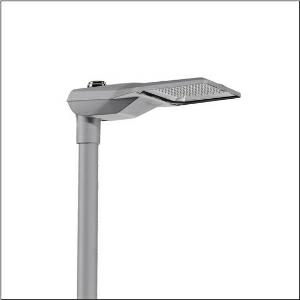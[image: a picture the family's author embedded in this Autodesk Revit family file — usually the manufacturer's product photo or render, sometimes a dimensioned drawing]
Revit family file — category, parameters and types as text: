
# Revit family: streetlight_sl_21_midi___p0_8a_5xe7u47n08lb_d940
name_source: partatom
category: Lighting Fixtures
units: mm (PartAtom-declared; Revit-internal decimal feet)

## family parameters
Cut with Voids When Loaded = No
Host = Face
Light Source = No
Part Type = Normal
Room Calculation Point = No
Round Connector Dimension = Use Diameter
Shared = No

## types (1)
- --- (1 x LED, 15080 lm, 98.3 W, 4000K)
    Apparent Load = 98 VA
    CIE Flux Codes = 33 69 96 100 100
    Color Rendering = 70
    Color Temperature = 4000K
    Default Elevation = 1800 mm
    Description = Streetlight SL 21 midi, mast luminaire, primary light control with lens, of PMMA, primary optical cover: cover, of toughened safety glass, transparent, light distribution: P0.8a, light emission: direct distribution, primary light characteristic: asymmetric, installation type: side-entry, LED, 3G 2.5mm², High Power LED, rated luminous flux: 15.080lm, luminous efficacy: 153lm/W, light colour: 740, colour temperature: 4000K, control gear: NEMA (7pin), control: flexible luminous flux parameterisation, time-dependent luminous flux control, constant luminous flux control, pre-setting: linear dimming characteristic, overheat protection, mains connection: 220..240V, AC, 50/60Hz, connection cable pre-assembled, cable length: 10,5m, wiring characteristics: H05VV-F, start of lifetime: 98W, end of service life: 101W, reduction: 45W, luminaire housing, of diecast aluminium (EN AC-44300), powder-coated, Siteco® metallic grey (DB 702S), corrosivity category C5 mid according to DIN EN ISO 12944, multi-level sealing system, sealing non-destructively replaceable, inclination adjustable: 0°, 5°, 10°, 15°, length: 644mm, width: 335mm, height: 110mm, spigot size: 42mm (side-entry), mounting height: 4..8m, protection rating (complete): IP66, insulation class (complete): insulation class I (protective earthing), certification: CE, ENEC, ENEC+, VDE, impact resistance: IK09, permissible operating ambient temperature for outdoor applications: -40..+50°C, standard-compliant lighting for roads and squares, packaging unit: 1 piece

Light Distribution: P0.8a
    Height = 111 mm
    Lamp = 1 x LED
    Lamp Light Flux = 15080 lm
    Lamp Power = 98.3 W
    Lamp count = 1
    Length = 644 mm
    Luminous efficacy = 153 lm/W
    Manufacturer = Siteco
    ModVariant = No
    Model = 5XE7U47N08LB
    Number of Poles = 1
    OnlyDefault = Yes
    Power Factor = 1
    Product Name = Streetlight SL 21 midi | P0.8a
    Product group = mast luminaire | pylon top
    ProductGroupID = 6100
    Protection Class = Protection class I
    Protection Degree = IP 66
    RLX_Detail_Level = 1
    RLX_Emergency_Light_Flux = 0 lm
    RLX_Emergency_Type = 0
    RLX_Emergency_Type_DB = No
    RlxData = <blob elided: 90185 chars, md5=269a2bb7>
    Socket = socket
    Standby Power = 0 W
    System Light Flux = 15080 lm
    System Power = 98 W
    Type Comments = factory setting: luminous flux: 100 % | dim-lin: 254 | 1020 mA
    Type Image = l_1294377.jpg
    URL = http://relux.com
    VarID = @adj_070274
    Voltage = 0 V
    Weight = 0.00 kg
    Width = 336 mm

## geometry (parser evidence)
native form markers: Blend x4, Sweep x11
no freeform markers — native parametric forms only
